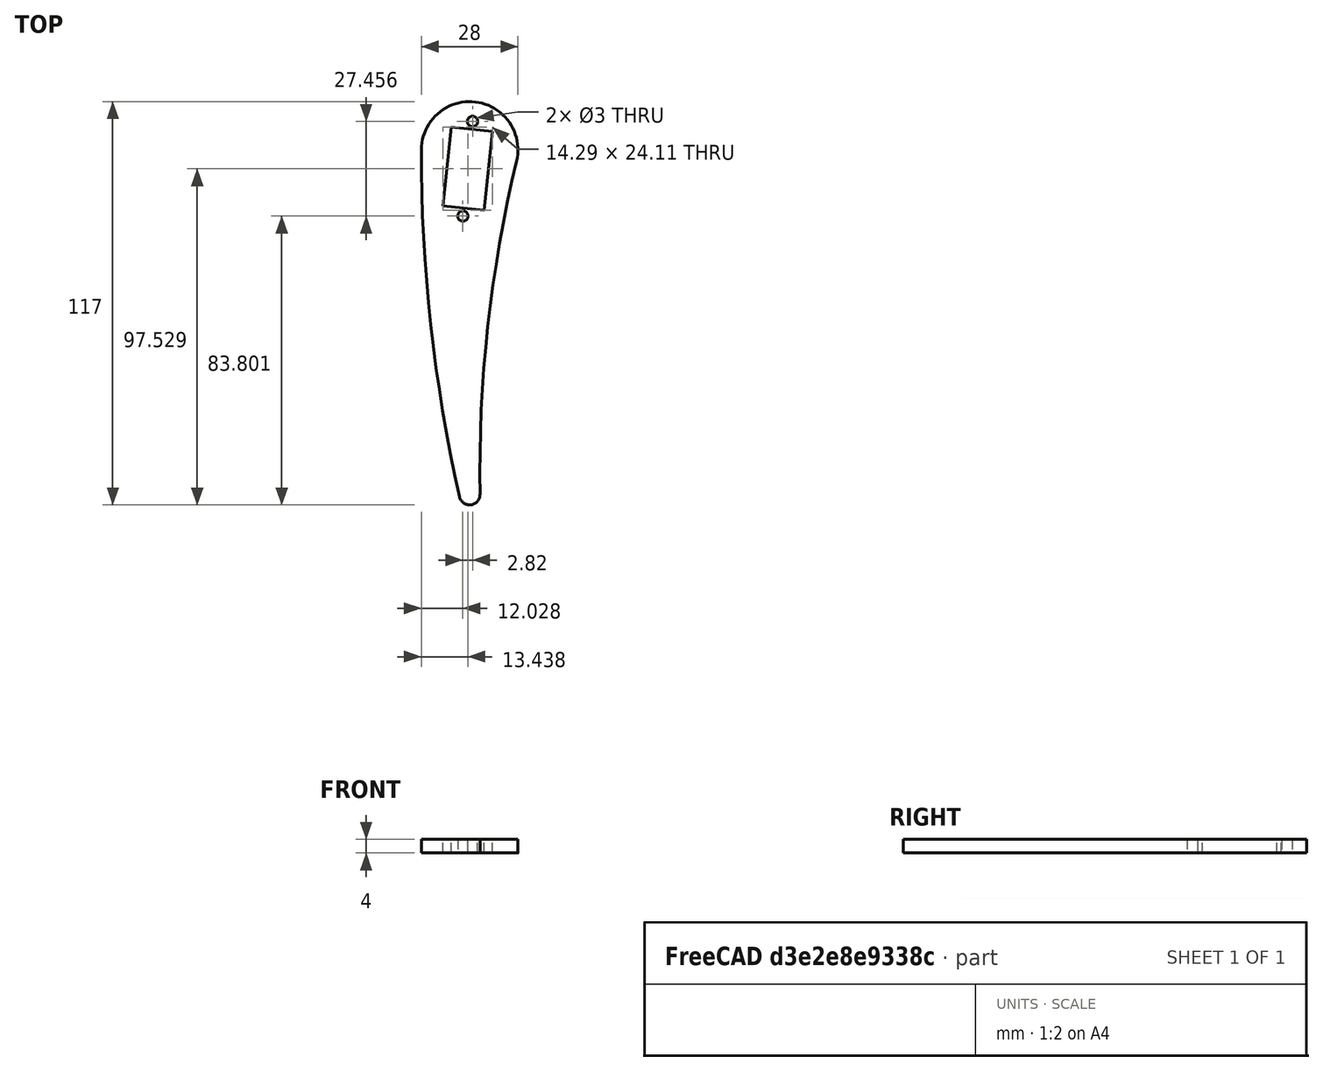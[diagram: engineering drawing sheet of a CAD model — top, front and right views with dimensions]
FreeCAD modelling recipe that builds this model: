
FCSTD DOCUMENT  (FreeCAD 0.16R6706 (Git))
Label: tibia
License: All rights reserved
LicenseURL: http://en.wikipedia.org/wiki/All_rights_reserved
objects: Sketcher::SketchObject×1, PartDesign::Pad×1
note: 3 computed .brp shape members not serialized (recipe doc carries the construction recipe); baked Part::Feature solids carry a one-line shape summary decoded from their .brp

FEATURE [Sketcher::SketchObject] Sketch
  sketch-geometry (10):
    g0: ArcOfCircle CenterX=0 CenterY=100 CenterZ=0 NormalX=0 NormalY=0 NormalZ=1 Radius=14 StartAngle=6.04836 EndAngle=9.42198
    g1: ArcOfCircle CenterX=391.593 CenterY=6.3142 CenterZ=0 NormalX=0 NormalY=0 NormalZ=1 Radius=388.644 StartAngle=2.90676 EndAngle=3.15772
    g2: ArcOfCircle CenterX=0 CenterY=0 CenterZ=0 NormalX=0 NormalY=0 NormalZ=1 Radius=3 StartAngle=3.36344 EndAngle=6.29931
    g3: ArcOfCircle CenterX=437.9 CenterY=98.7742 CenterZ=0 NormalX=0 NormalY=0 NormalZ=1 Radius=451.902 StartAngle=3.13879 EndAngle=3.36344
    g4: LineSegment StartX=-5.35557 StartY=106.582 StartZ=0 EndX=6.58163 EndY=105.356 EndZ=0
    g5: LineSegment StartX=6.58163 StartY=105.356 StartZ=0 EndX=4.23169 EndY=82.4759 EndZ=0
    g6: LineSegment StartX=4.23169 StartY=82.4759 StartZ=0 EndX=-7.70551 EndY=83.702 EndZ=0
    g7: LineSegment StartX=-7.70551 StartY=83.702 StartZ=0 EndX=-5.35557 EndY=106.582 EndZ=0
    g8: Circle CenterX=0.848022 CenterY=108.257 CenterZ=0 NormalX=0 NormalY=0 NormalZ=1 Radius=1.5
    g9: Circle CenterX=-1.97191 CenterY=80.801 CenterZ=0 NormalX=0 NormalY=0 NormalZ=1 Radius=1.5
  constraints (30):
    c: Coincident(g1,g0)
    c: Coincident(g3,g2)
    c: Coincident(g0,g3)
    c: Tangent(g2,g1)
    c: Coincident(g1,g2)
    c: Radius(g2) = 3
    c: Tangent(g1,g0)
    c: Radius(g0) = 14
    c: Tangent(g3,g0)
    c: Tangent(g2,g3)
    c: Coincident(g4,g5)
    c: Coincident(g5,g6)
    c: Coincident(g6,g7)
    c: Coincident(g7,g4)
    c: Parallel(g7,g5)
    c: Parallel(g6,g4)
    c: Perpendicular(g6,g7)
    c: Distance(g4,g5) = 12
    c: Distance(g4,g6) = 23
    c: Distance(g0,g5) = 6
    c: Coincident(g2,g-1)
    c: PointOnObject(g0,g-2)
    c: Distance(g0,g4) = 6
    c: Distance(g-1,g0) = 100
    c: Radius(g8) = 1.5
    c: Distance(g8,g5) = 6
    c: Distance(g8,g4) = 2.3
    c: Radius(g9) = 1.5
    c: Distance(g9,g6) = 2.3
    c: Distance(g9,g5) = 6
FEATURE [PartDesign::Pad] Pad
  Length = 4
  Length2 = 100
  Sketch = -> Sketch
  Type = 0
